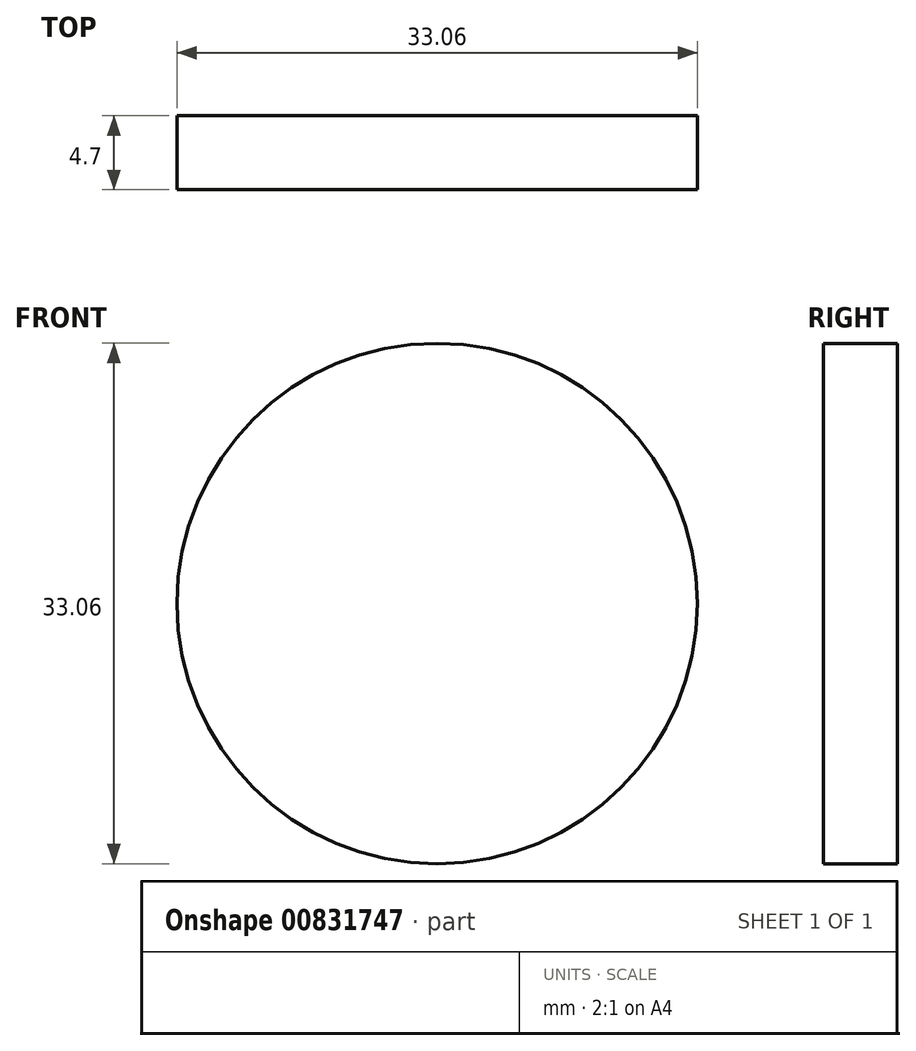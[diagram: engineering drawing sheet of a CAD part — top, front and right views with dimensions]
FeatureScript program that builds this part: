
annotation { "Feature Type Name" : "Feature", "Feature Type Description" : "" }
export const myFeature = defineFeature(function(context is Context, id is Id, definition is map)
    precondition{}
    {
        {
            var Q0;
            Q0=qCreatedBy(makeId("Front.planeOp"),FACE);
            var sketch = newSketch(context, id + "F0", { "sketchPlane" : qUnion([Q0])});
            skCircle(sketch, "E0", {"center": v(0, 0) * mm, "radius": 16.53 * mm});
            skSolve(sketch);
        }
        {
            var Q0;
            Q0=makeQuery(id+"F0.imprint","IMPRINT",FACE,{"disambiguationData":[TD([[makeQuery(id+"F0.imprint","IMPRINT",EDGE,{"derivedFrom":sQuery(id+"F0.wireOp",EDGE,"E0")}),1.0]])]});
            extrude(context, id + "F1", {"entities" : qUnion([Q0]), "depth" : 4.7 * mm, "offsetDistance" : 25 * mm});
        }
    });
